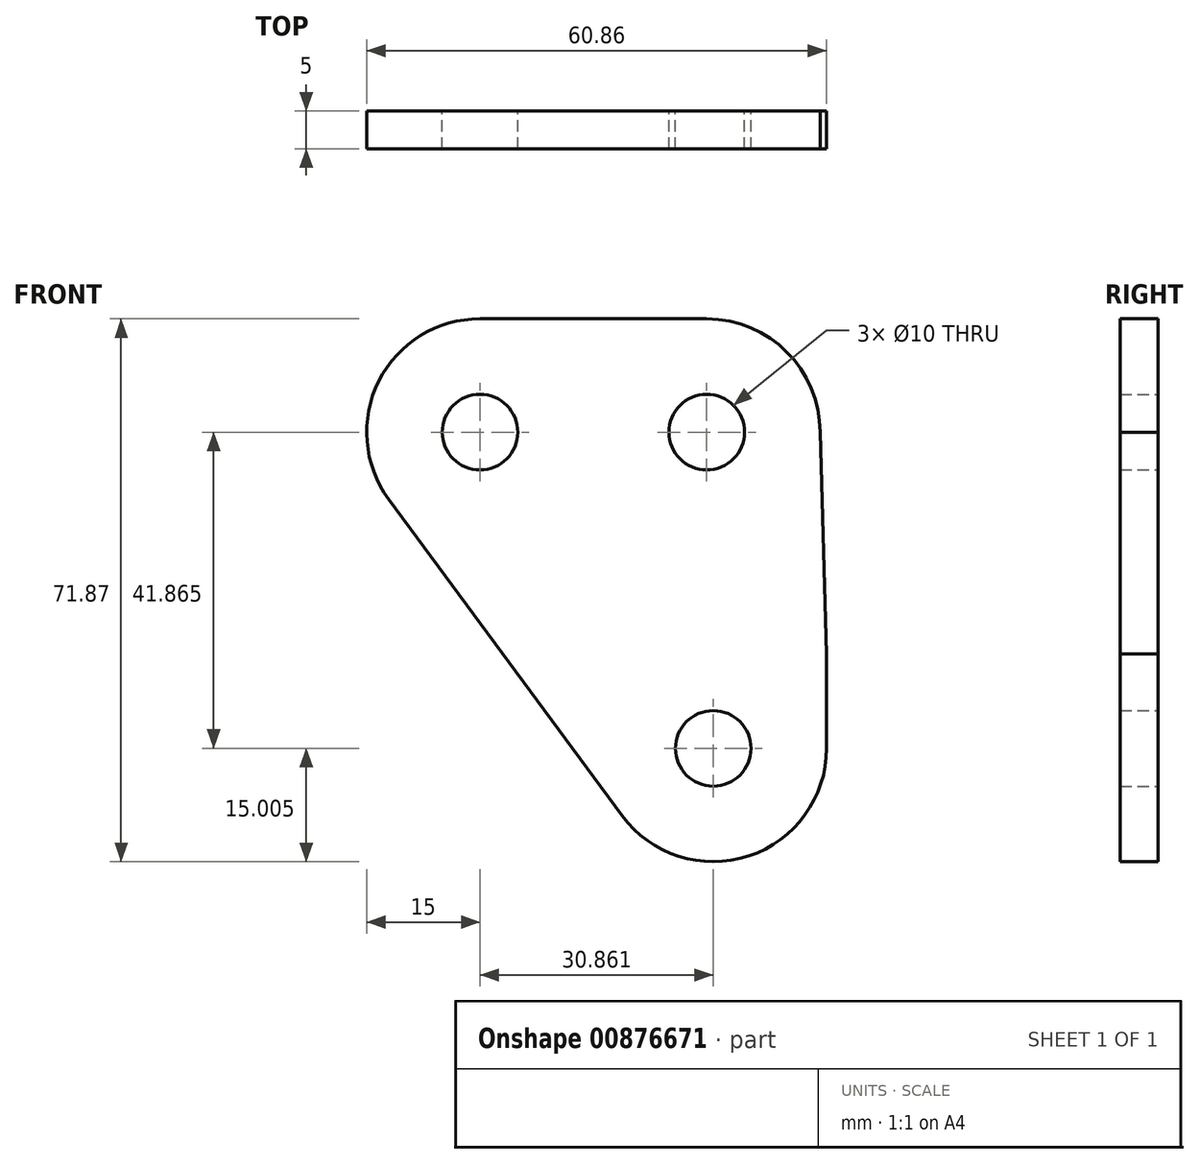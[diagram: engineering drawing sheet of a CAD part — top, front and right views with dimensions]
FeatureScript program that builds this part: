
annotation { "Feature Type Name" : "Feature", "Feature Type Description" : "" }
export const myFeature = defineFeature(function(context is Context, id is Id, definition is map)
    precondition{}
    {
        {
            var Q0;
            Q0=qCreatedBy(makeId("Front.planeOp"),FACE);
            var sketch = newSketch(context, id + "F0", { "sketchPlane" : qUnion([Q0])});
            skLineSegment(sketch, "E0.bottom", {"start": v(15, 0) * mm, "end": v(45, 0) * mm});
            skLineSegment(sketch, "E0.right", {"start": v(60, -15) * mm, "end": v(60.86, -44.37) * mm});
            skCircle(sketch, "E1", {"center": v(45, -15) * mm, "radius": 5 * mm});
            skCircle(sketch, "E2", {"center": v(15, -15) * mm, "radius": 5 * mm});
            skArc(sketch, "E3", {"start": v(15, 0) * mm, "mid": v(1.61, -8.24) * mm, "end": v(2.93, -23.9) * mm});
            skArc(sketch, "E4", {"start": v(60, -15) * mm, "mid": v(55.6, -4.4) * mm, "end": v(45, 0) * mm});
            skLineSegment(sketch, "E5", {"start": v(60.86, -44.37) * mm, "end": v(60.86, -56.87) * mm});
            skCircle(sketch, "E6", {"center": v(45.86, -56.87) * mm, "radius": 5 * mm});
            skArc(sketch, "E7", {"start": v(33.79, -65.77) * mm, "mid": v(50.55, -71.11) * mm, "end": v(60.86, -56.87) * mm});
            skLineSegment(sketch, "E8", {"start": v(33.79, -65.77) * mm, "end": v(2.93, -23.9) * mm});
            skSolve(sketch);
        }
        {
            var Q0;
            Q0=makeQuery(id+"F0.imprint","IMPRINT",FACE,{"disambiguationData":[TD([[makeQuery(id+"F0.imprint","IMPRINT",EDGE,{"derivedFrom":sQuery(id+"F0.wireOp",EDGE,"E0.bottom")}),-1.0]])]});
            extrude(context, id + "F1", {"entities" : qUnion([Q0]), "depth" : 5 * mm, "offsetDistance" : 25 * mm});
        }
    });
